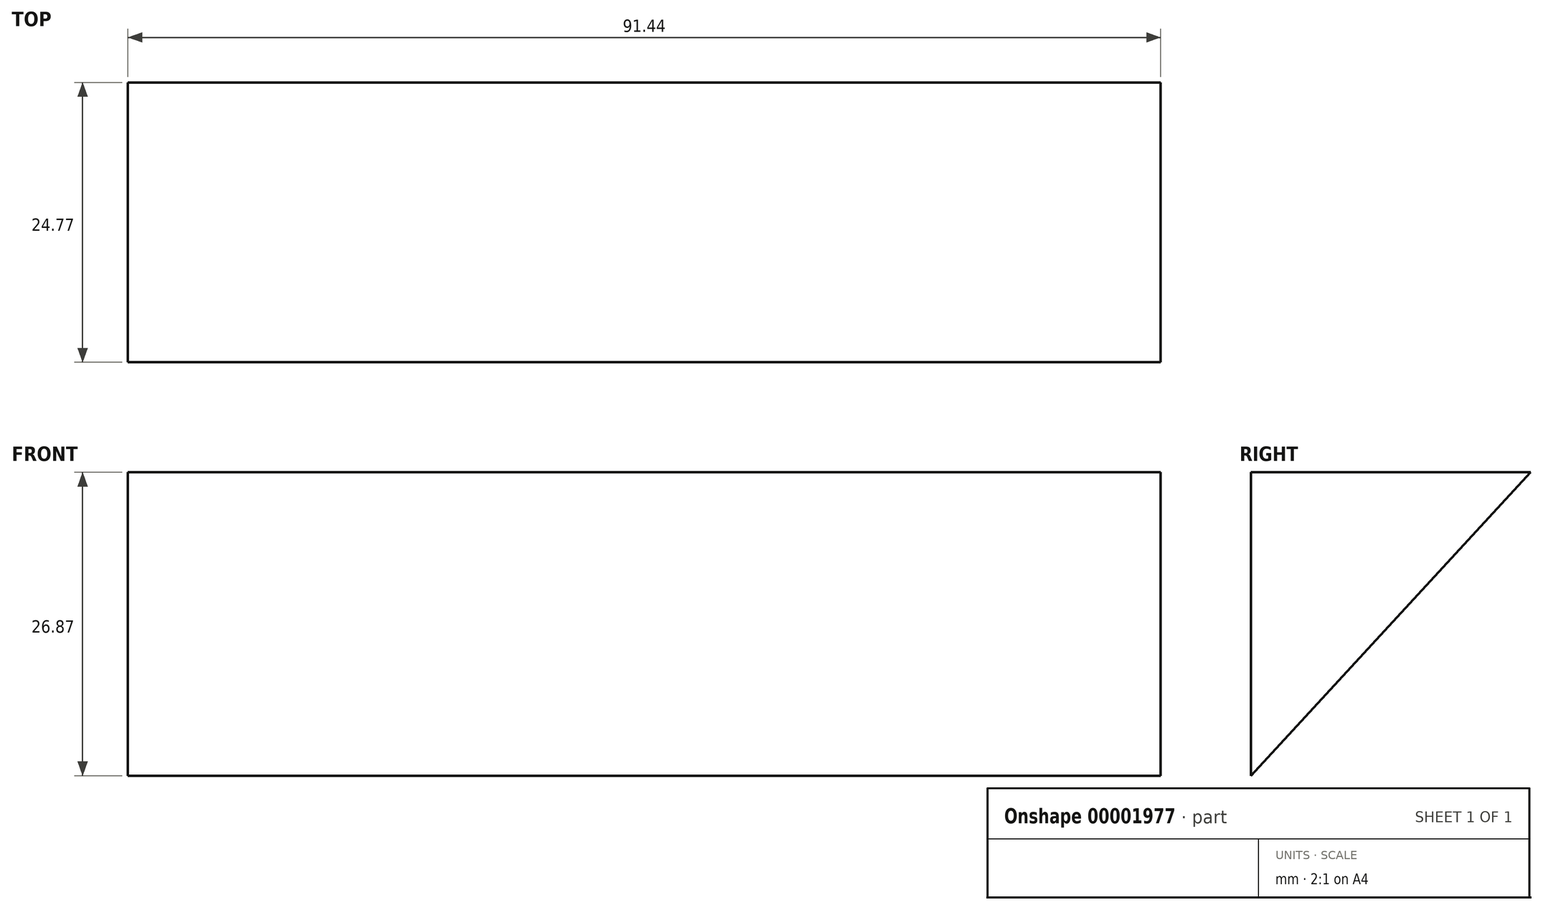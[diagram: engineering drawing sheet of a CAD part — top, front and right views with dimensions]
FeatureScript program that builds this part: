
annotation { "Feature Type Name" : "Feature", "Feature Type Description" : "" }
export const myFeature = defineFeature(function(context is Context, id is Id, definition is map)
    precondition{}
    {
        {
            var Q0;
            Q0=qCreatedBy(makeId("Right.planeOp"),FACE);
            var sketch = newSketch(context, id + "F0", { "sketchPlane" : qUnion([Q0])});
            skLineSegment(sketch, "E0", {"start": v(0, -26.87) * mm, "end": v(0, 0) * mm});
            skLineSegment(sketch, "E1", {"start": v(0, -26.87) * mm, "end": v(24.77, 0) * mm});
            skLineSegment(sketch, "E2", {"start": v(24.77, 0) * mm, "end": v(0, 0) * mm});
            skSolve(sketch);
        }
        {
            var Q0;
            Q0=makeQuery(id+"F0.imprint","IMPRINT",FACE,{"disambiguationData":[TD([[makeQuery(id+"F0.imprint","IMPRINT",EDGE,{"derivedFrom":sQuery(id+"F0.wireOp",EDGE,"E0")}),-1.0]])]});
            extrude(context, id + "F1", {"entities" : qUnion([Q0]), "depth" : 91.44 * mm});
        }
    });
